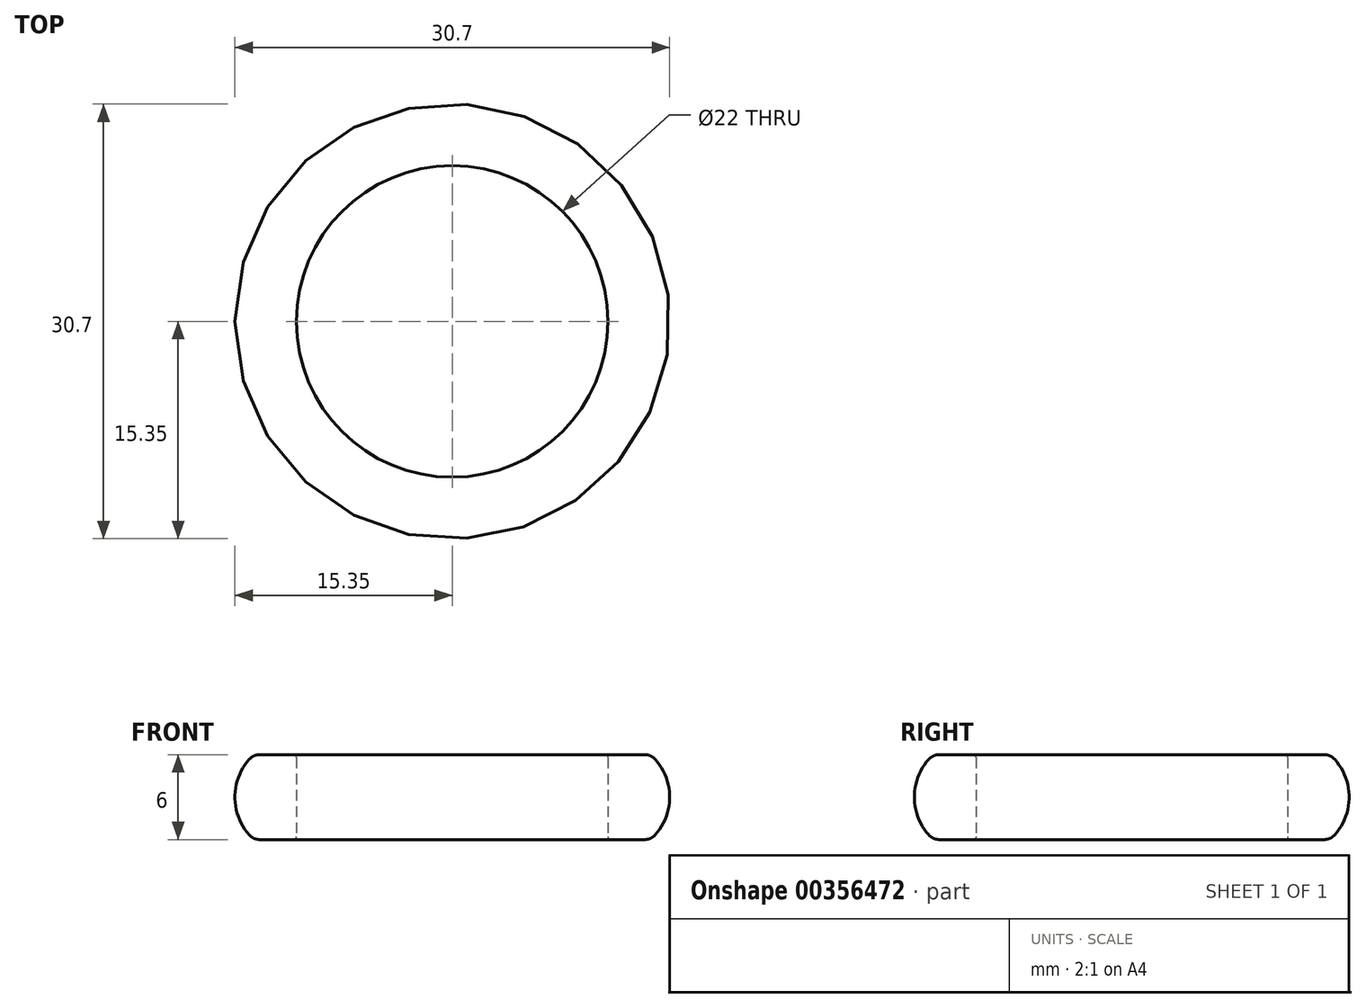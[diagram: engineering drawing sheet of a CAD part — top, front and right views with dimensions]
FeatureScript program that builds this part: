
annotation { "Feature Type Name" : "Feature", "Feature Type Description" : "" }
export const myFeature = defineFeature(function(context is Context, id is Id, definition is map)
    precondition{}
    {
        {
            var Q0;
            Q0=qCreatedBy(makeId("Front.planeOp"),FACE);
            var sketch = newSketch(context, id + "F0", { "sketchPlane" : qUnion([Q0])});
            skLineSegment(sketch, "E0", {"start": v(0, 0.2) * mm, "end": v(0, 5.8) * mm});
            skLineSegment(sketch, "E1", {"start": v(-0.2, 0) * mm, "end": v(-2.6, 0) * mm});
            skLineSegment(sketch, "E2", {"start": v(-0.2, 6) * mm, "end": v(-2.6, 6) * mm});
            skArc(sketch, "E3", {"start": v(-3.34, 5.67) * mm, "mid": v(-4.35, 3) * mm, "end": v(-3.34, 0.33) * mm});
            skPoint(sketch, "E4.visualSharp", {"position": v(-3, 6) * mm});
            skArc(sketch, "E4.filletArc", {"start": v(-2.6, 6) * mm, "mid": v(-3, 5.91) * mm, "end": v(-3.34, 5.67) * mm});
            skPoint(sketch, "E5.visualSharp", {"position": v(-3, 0) * mm});
            skArc(sketch, "E5.filletArc", {"start": v(-3.34, 0.33) * mm, "mid": v(-3, 0.09) * mm, "end": v(-2.6, 0) * mm});
            skPoint(sketch, "E6.visualSharp", {"position": v(0, 0) * mm});
            skArc(sketch, "E6.filletArc", {"start": v(-0.2, 0) * mm, "mid": v(-0.06, 0.06) * mm, "end": v(0, 0.2) * mm});
            skPoint(sketch, "E7.visualSharp", {"position": v(0, 6) * mm});
            skArc(sketch, "E7.filletArc", {"start": v(0, 5.8) * mm, "mid": v(-0.06, 5.94) * mm, "end": v(-0.2, 6) * mm});
            skLineSegment(sketch, "E8.0", {"start": v(11, 0.2) * mm, "end": v(11, 5.8) * mm});
            skSolve(sketch);
        }
        {
            var Q0;
            Q0=makeQuery(id+"F0.imprint","IMPRINT",FACE,{"disambiguationData":[TD([[makeQuery(id+"F0.imprint","IMPRINT",EDGE,{"derivedFrom":sQuery(id+"F0.wireOp",EDGE,"E0")}),1.0]])]});
            var Q1;
            Q1=sQuery(id+"F0.wireOp",EDGE,"E8.0");
            revolve(context, id + "F1", {"entities" : qUnion([Q0]), "axis" : qUnion([Q1]), "revolveType" : RevolveType.FULL});
        }
    });
